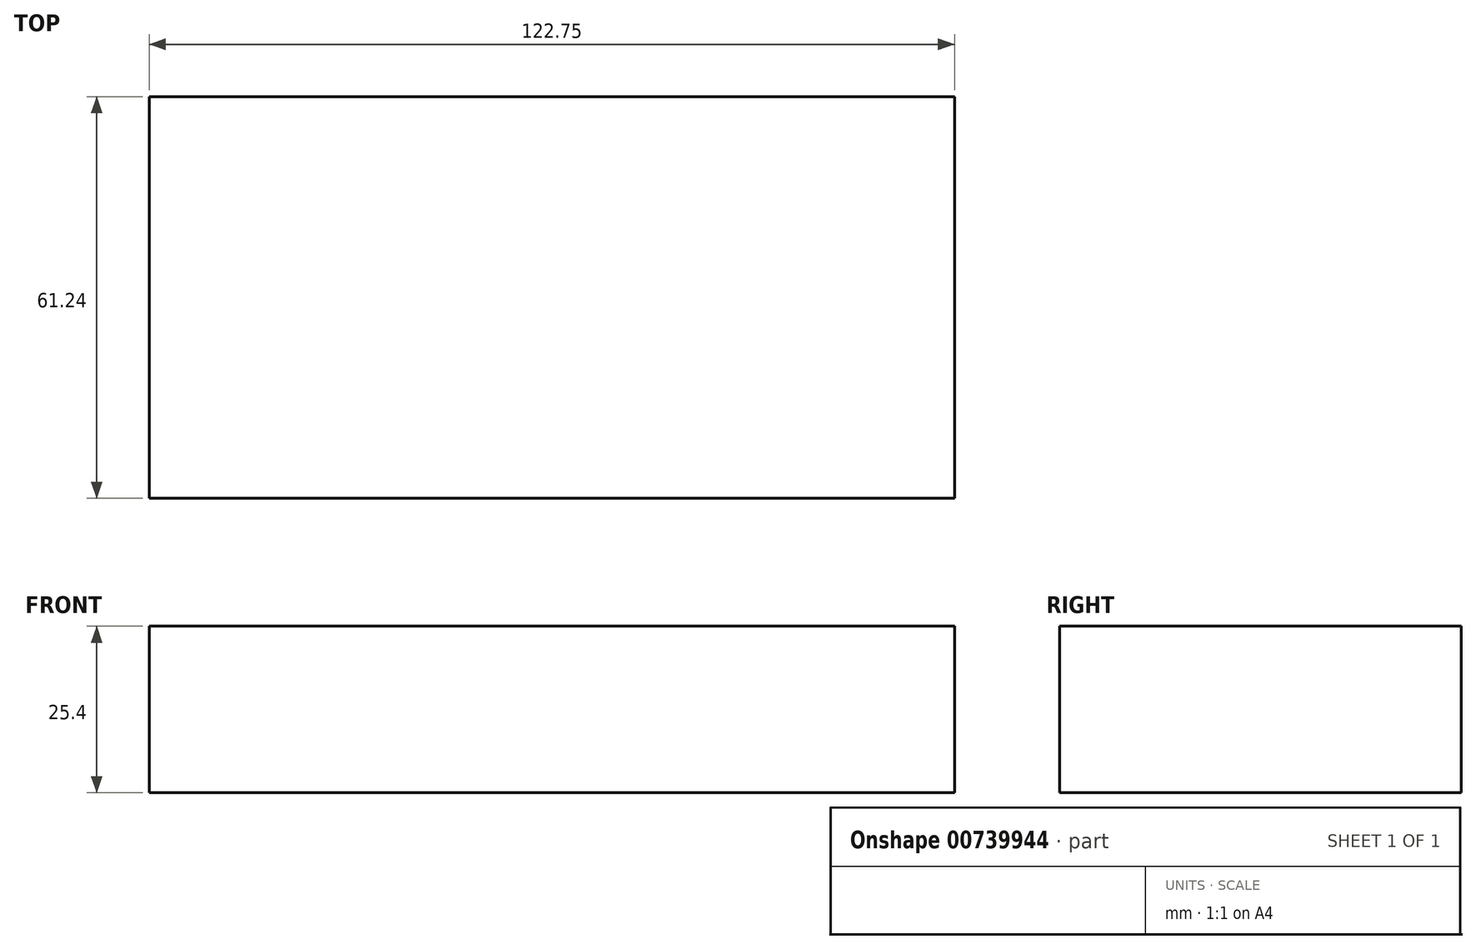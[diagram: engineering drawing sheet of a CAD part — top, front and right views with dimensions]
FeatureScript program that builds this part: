
annotation { "Feature Type Name" : "Feature", "Feature Type Description" : "" }
export const myFeature = defineFeature(function(context is Context, id is Id, definition is map)
    precondition{}
    {
        {
            var Q0;
            Q0=qCreatedBy(makeId("Top.planeOp"),FACE);
            var sketch = newSketch(context, id + "F0", { "sketchPlane" : qUnion([Q0])});
            skLineSegment(sketch, "E0.bottom", {"start": v(-59.5, -30.09) * mm, "end": v(63.24, -30.09) * mm});
            skLineSegment(sketch, "E0.top", {"start": v(-59.5, 31.15) * mm, "end": v(63.24, 31.15) * mm});
            skLineSegment(sketch, "E0.left", {"start": v(-59.5, 31.15) * mm, "end": v(-59.5, -30.09) * mm});
            skLineSegment(sketch, "E0.right", {"start": v(63.24, 31.15) * mm, "end": v(63.24, -30.09) * mm});
            skSolve(sketch);
        }
        {
            var Q0;
            Q0 = qSketchRegion(id + "F0", true);
            extrude(context, id + "F1", {"entities" : qUnion([Q0]), "depth" : 25.4 * mm, "offsetDistance" : 25.4 * mm});
        }
    });
